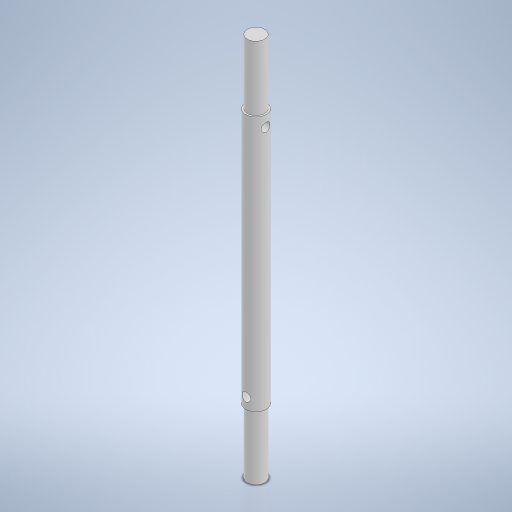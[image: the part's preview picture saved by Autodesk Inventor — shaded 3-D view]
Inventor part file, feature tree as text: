
AUTODESK INVENTOR PART (.ipt)
format: ipt  version: 2024 (Build 280153000, 153)  size: 266,240 bytes
history: native  units: mm
features: sketch x3, plane x2, hole x2, revolve x1
ambient origin geometry x8: Origin, YZ Plane, XZ Plane, XY Plane, X Axis, Y Axis, Z Axis, Center Point
bodies: Volumenkörper1 (feature_tree)
feature tree (8):
  revolve  "Umdrehung1"
  plane  "Arbeitsebene1"
  hole  "Bohrung1"  [1 undecoded]
  plane  "Arbeitsebene2"
  hole  "Bohrung2"  [1 undecoded]
  sketch  "Skizze1"  dims[d0=16.0mm d1=59.0mm]
  sketch  "Skizze2"  dims[d2=59.0mm d3=352.0mm]
  sketch  "Skizze3"  dims[d4=19.0mm d5=90.0deg d6=9.5mm d7=69.0mm d8=8.0mm d9=20.0mm d10=4.0mm d11=2.0mm d12=90.0deg d13=8.0mm d14=0.0mm d15=9.5mm d16=10.0mm d17=8.0mm d18=6.0mm d19=4.0mm d20=2.0mm d21=90.0deg d22=8.0mm d23=0.0mm]
note: 2 required parameter values undecoded (feature->parameter linkage not recoverable at this tier; creation-order binding heuristic only, values carry confidence <= 0.55)
